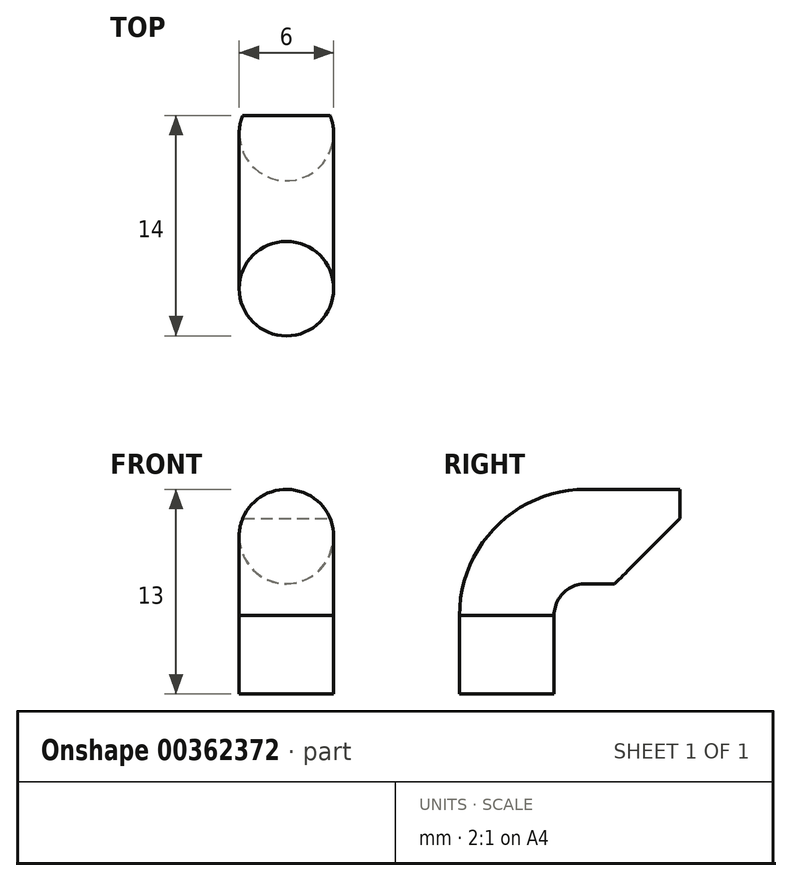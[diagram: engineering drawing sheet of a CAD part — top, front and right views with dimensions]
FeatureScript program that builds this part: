
annotation { "Feature Type Name" : "Feature", "Feature Type Description" : "" }
export const myFeature = defineFeature(function(context is Context, id is Id, definition is map)
    precondition{}
    {
        {
            var Q0;
            Q0=qCreatedBy(makeId("Right.planeOp"),FACE);
            var sketch = newSketch(context, id + "F0", { "sketchPlane" : qUnion([Q0])});
            skLineSegment(sketch, "E0.left", {"start": v(0, 0) * mm, "end": v(0, 5) * mm});
            skPoint(sketch, "E0.middle", {"position": v(0, 0) * mm});
            skArc(sketch, "E1", {"start": v(5, 10) * mm, "mid": v(1.46, 8.54) * mm, "end": v(0, 5) * mm});
            skLineSegment(sketch, "E2", {"start": v(5, 10) * mm, "end": v(11, 10) * mm});
            skSolve(sketch);
        }
        {
            var Q0;
            Q0=qCreatedBy(makeId("Top.planeOp"),FACE);
            var sketch = newSketch(context, id + "F1", { "sketchPlane" : qUnion([Q0])});
            skCircle(sketch, "E3", {"center": v(0, 0) * mm, "radius": 3 * mm});
            skSolve(sketch);
        }
        {
            var Q0;
            Q0=makeQuery(id+"F1.imprint","IMPRINT",FACE,{"disambiguationData":[TD([[makeQuery(id+"F1.imprint","IMPRINT",EDGE,{"derivedFrom":sQuery(id+"F1.wireOp",EDGE,"E3")}),1.0]])]});
            var Q1;
            Q1=sQuery(id+"F0.wireOp",EDGE,"E0.left");
            var Q2;
            Q2=sQuery(id+"F0.wireOp",EDGE,"E1");
            var Q3;
            Q3=sQuery(id+"F0.wireOp",EDGE,"E2");
            sweep(context, id + "F2", {"profiles" : qUnion([Q0]), "path" : qUnion([Q1, Q2, Q3])});
        }
        {
            var Q0;
            Q0=qCreatedBy(makeId("Right.planeOp"),FACE);
            var sketch = newSketch(context, id + "F3", { "sketchPlane" : qUnion([Q0])});
            skLineSegment(sketch, "E4", {"start": v(11, 13) * mm, "end": v(5, 13) * mm});
            skLineSegment(sketch, "E5", {"start": v(5, 7) * mm, "end": v(11, 7) * mm});
            skLineSegment(sketch, "E6", {"start": v(11, 11.16) * mm, "end": v(6.84, 7) * mm});
            skLineSegment(sketch, "E7", {"start": v(11, 7) * mm, "end": v(6.84, 7) * mm});
            skLineSegment(sketch, "E8", {"start": v(11, 7) * mm, "end": v(11, 11.16) * mm});
            skSolve(sketch);
        }
        {
            var Q0;
            Q0 = qSketchRegion(id + "F3", true);
            extrude(context, id + "F4", {"entities" : qUnion([Q0]), "operationType" : NewBodyOperationType.REMOVE, "endBound" : BoundingType.SYMMETRIC, "oppositeDirection" : true, "depth" : 25 * mm});
        }
        {
            var Q0;
            Q0=makeQuery(id+"F1.imprint","IMPRINT",FACE,{"disambiguationData":[TD([[makeQuery(id+"F1.imprint","IMPRINT",EDGE,{"derivedFrom":sQuery(id+"F1.wireOp",EDGE,"E3")}),1.0]])]});
            var Q1;
            Q1=sQuery(id+"F0.wireOp",EDGE,"E0.left");
            sweep(context, id + "F5", {"profiles" : qUnion([Q0]), "path" : qUnion([Q1])});
        }
    });
